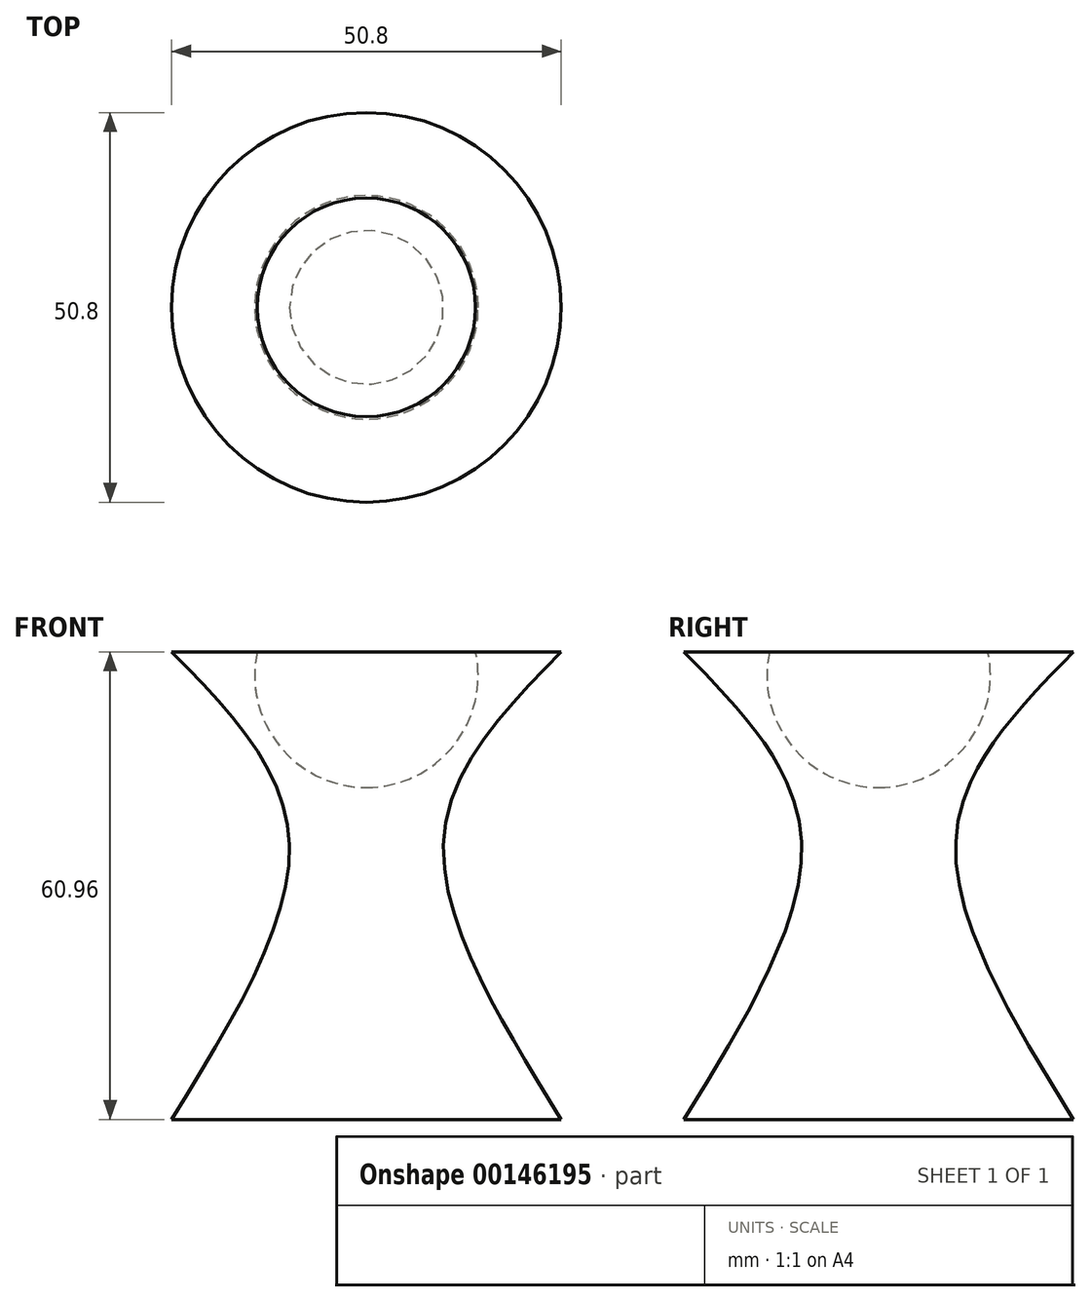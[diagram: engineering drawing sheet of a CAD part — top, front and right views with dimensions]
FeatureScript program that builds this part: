
annotation { "Feature Type Name" : "Feature", "Feature Type Description" : "" }
export const myFeature = defineFeature(function(context is Context, id is Id, definition is map)
    precondition{}
    {
        {
            var Q0;
            Q0=qCreatedBy(makeId("Top.planeOp"),FACE);
            var sketch = newSketch(context, id + "F0", { "sketchPlane" : qUnion([Q0])});
            skCircle(sketch, "E0", {"center": v(0, 0) * mm, "radius": 25.4 * mm});
            skSolve(sketch);
        }
        {
            var Q0;
            Q0 = qSketchRegion(id + "F0", true);
            extrude(context, id + "F1", {"entities" : qUnion([Q0]), "depth" : 60.96 * mm});
        }
        {
            var Q0;
            Q0=qCreatedBy(makeId("Front.planeOp"),FACE);
            var sketch = newSketch(context, id + "F2", { "sketchPlane" : qUnion([Q0])});
            skLineSegment(sketch, "E1", {"start": v(-25.4, 73.46) * mm, "end": v(-25.4, -16.1) * mm, "construction": true});
            skLineSegment(sketch, "E2", {"start": v(0, 69.74) * mm, "end": v(0, -20.04) * mm, "construction": true});
            skLineSegment(sketch, "E3", {"start": v(-36.35, 60.96) * mm, "end": v(45.98, 60.96) * mm, "construction": true});
            skFitSpline(sketch, "E4", {"points": [v(-25.4, 60.96) * mm, v(-10.11, 37.05) * mm, v(-25.4, 0) * mm], "startDerivative": vector(47.53, -48.68) * mm, "endDerivative": vector(-44.87, -72.55) * mm});
            skLineSegment(sketch, "E5", {"start": v(-25.4, 60.96) * mm, "end": v(-25.4, 0) * mm});
            skSolve(sketch);
        }
        {
            var Q0;
            Q0 = qSketchRegion(id + "F2", true);
            var Q1;
            Q1=sQuery(id+"F2.wireOp",EDGE,"E2");
            revolve(context, id + "F3", {"operationType" : NewBodyOperationType.REMOVE, "entities" : qUnion([Q0]), "axis" : qUnion([Q1]), "revolveType" : RevolveType.FULL, "oppositeDirection" : true});
        }
        {
            var Q0;
            Q0=qCreatedBy(makeId("Front.planeOp"),FACE);
            var sketch = newSketch(context, id + "F4", { "sketchPlane" : qUnion([Q0])});
            skArc(sketch, "E6", {"start": v(0, 43.28) * mm, "mid": v(14.57, 57.85) * mm, "end": v(0, 72.42) * mm});
            skLineSegment(sketch, "E7", {"start": v(0, 72.42) * mm, "end": v(0, 43.28) * mm});
            skSolve(sketch);
        }
        {
            var Q0;
            Q0 = qSketchRegion(id + "F4", true);
            var Q1;
            Q1=sQuery(id+"F4.wireOp",EDGE,"E7");
            revolve(context, id + "F5", {"operationType" : NewBodyOperationType.REMOVE, "entities" : qUnion([Q0]), "axis" : qUnion([Q1]), "revolveType" : RevolveType.FULL, "oppositeDirection" : true});
        }
    });
